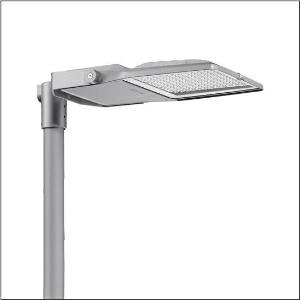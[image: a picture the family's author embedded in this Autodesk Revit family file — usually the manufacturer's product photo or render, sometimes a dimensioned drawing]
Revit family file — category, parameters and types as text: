
# Revit family: floodlight_fl_21_midi___pl61_5xa7786e2c3a_519c
name_source: partatom
category: Lighting Fixtures
units: mm (PartAtom-declared; Revit-internal decimal feet)

## family parameters
Cut with Voids When Loaded = No
Host = Face
Light Source = No
Part Type = Normal
Room Calculation Point = No
Round Connector Dimension = Use Diameter
Shared = No

## types (1)
- --- (1 x LED, 26450 lm, 212.4 W, 3000K)
    Apparent Load = 212 VA
    CIE Flux Codes = 33 65 98 100 100
    Color Rendering = 70
    Color Temperature = 3000K
    Default Elevation = 1800 mm
    Description = Floodlight FL 21 midi, floodlight, primary light control with lens, of PMMA, primary optical cover: protective disc, of toughened safety glass, transparent, light distribution: PL61, light emission: direct distribution, installation type: surface-mounted, LED, High Power LED, rated luminous flux: 26.450lm, luminous efficacy: 125lm/W, light colour: 730, colour temperature: 3000K, control gear: ECG Smart Interface, control: flexible luminous flux parameterisation, time-dependent luminous flux control, constant luminous flux control, overheat protection, presetting dimming logarithmic, with terminal, 6-pole, mains connection: 220..240V, AC, 50/60Hz, start of lifetime: 212W, end of service life: 231W, reduction: 95W, luminaire housing, of diecast aluminium, powder-coated, Siteco® metallic grey (DB 702S), corrosivity category C5 mid according to DIN EN ISO 12944, sealing non-destructively replaceable, please order mast flange separately, mast bracket, of steel, galvanised, powder-coated, Siteco® metallic grey (DB 702S), Smart Interface below and above, protection rating (complete): IP66, insulation class (complete): insulation class II (safety insulation), certification: CE, protection symbol: D, impact resistance: IK08, permissible operating ambient temperature: -40..+40°C, permissible operating ambient temperature for outdoor applications: -40..+50°C, standard: DIN EN 12944, LABS conformity tested according to VDMA 24364:2018-05, packaging unit: 1 piece

Light Distribution: PL61
    Height = 76 mm
    Lamp = 1 x LED
    Lamp Light Flux = 26450 lm
    Lamp Power = 212.4 W
    Lamp count = 1
    Length = 657 mm
    Luminous efficacy = 125 lm/W
    Manufacturer = Siteco
    ModVariant = No
    Model = 5XA7786E2C3A
    Number of Poles = 1
    OnlyDefault = Yes
    Power Factor = 1
    Product Name = Floodlight FL 21 midi | PL61
    Product group = floodlight | pylon annexe
    ProductGroupID = 6200
    Protection Class = Protection class II
    Protection Degree = IP 66
    RLX_Detail_Level = 1
    RLX_Emergency_Light_Flux = 0 lm
    RLX_Emergency_Type = 0
    RLX_Emergency_Type_DB = No
    RlxData = <blob elided: 153637 chars, md5=a2a4d7e1>
    Socket = socket
    Standby Power = 0 W
    System Light Flux = 26450 lm
    System Power = 212 W
    Type Comments = factory setting: luminous flux: 100 % | dim-lin: 254 | 710 mA
    Type Image = l_1007123.jpg
    URL = http://relux.com
    VarID = @adj_146721
    Voltage = 0 V
    Weight = 0.00 kg
    Width = 442 mm

## geometry (parser evidence)
native form markers: Blend x4, Sweep x14
no freeform markers — native parametric forms only
